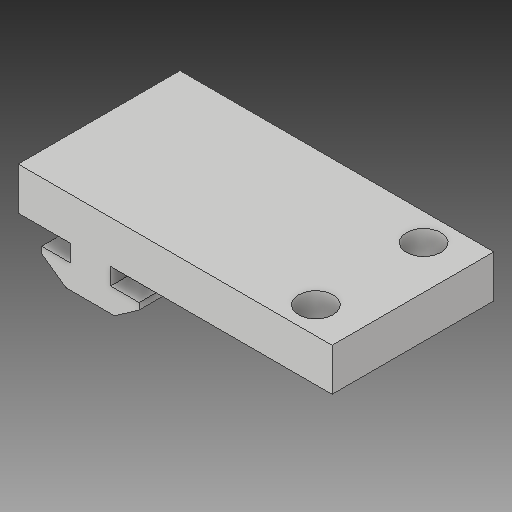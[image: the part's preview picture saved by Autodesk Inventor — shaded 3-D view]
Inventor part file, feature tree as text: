
AUTODESK INVENTOR PART (.ipt)
format: ipt  version: 2019 (Build 230136000, 136)  size: 125,952 bytes
history: native  units: in
note: dims shown in document units (in); Inventor stores cm internally (conversion verified against a paired STEP export)
features: sketch x2, extrude x1, hole x1
ambient origin geometry x8: Origin, YZ Plane, XZ Plane, XY Plane, X Axis, Y Axis, Z Axis, Center Point
bodies: Solid1 (feature_tree)
feature tree (4):
  extrude  "Extrusion1"  Depth=0.0787in
  hole  "Hole1"  [1 undecoded]
  sketch  "Sketch1"  dims[d0=0.6693in d2=0.1969in d3=0.0787in]
  sketch  "Sketch3"  dims[d4=0.1874in d6=0.4524in d7=0.1085in d8=0.225in d9=0.2221in d10=0.2409in d11=0.03in d12=0.03in d13=0.75in d14=0.0in d16=1.0268in d27=0.2in d28=0.2in d29=0.16in d30=0.75in d31=0.375in d32=0.25in d33=0.5635in d34=1.0in d35=0.8108in d36=0.125in d37=0.125in d50=0.9949in d51=0.1137in]
note: 1 required parameter value undecoded (feature->parameter linkage not recoverable at this tier; creation-order binding heuristic only, values carry confidence <= 0.55)
